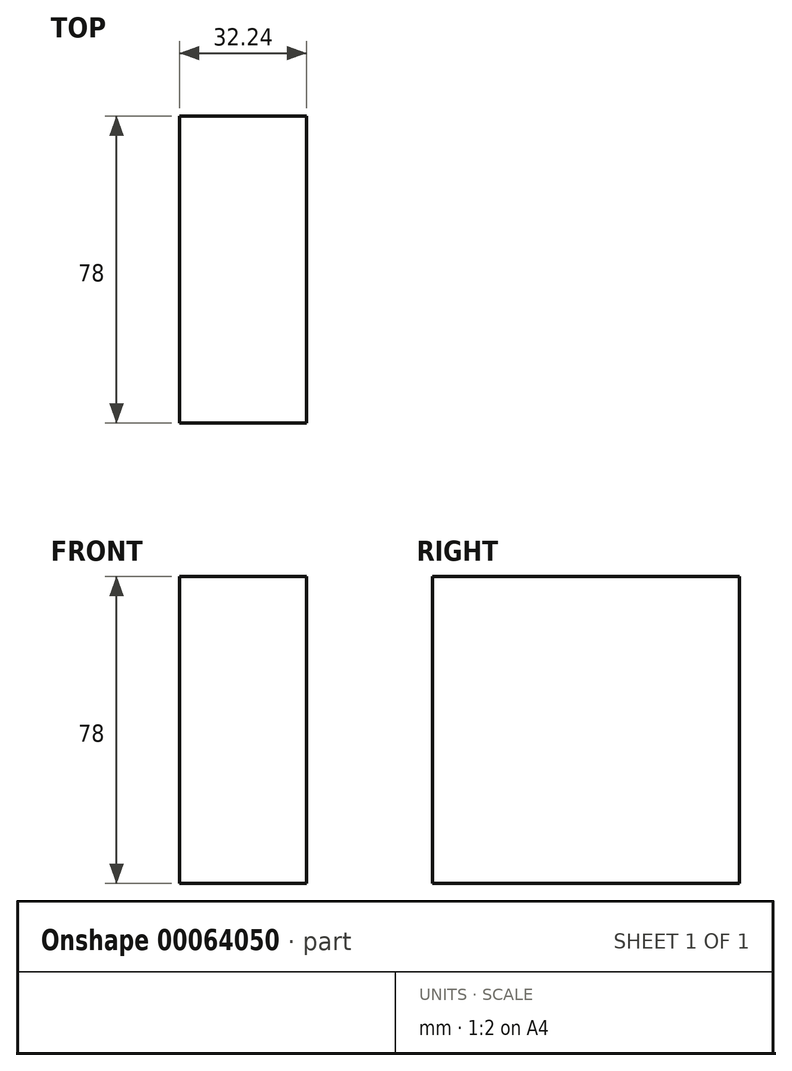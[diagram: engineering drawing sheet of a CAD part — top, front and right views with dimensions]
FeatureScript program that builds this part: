
annotation { "Feature Type Name" : "Feature", "Feature Type Description" : "" }
export const myFeature = defineFeature(function(context is Context, id is Id, definition is map)
    precondition{}
    {
        {
            var Q0;
            Q0=qCreatedBy(makeId("Right.planeOp"),FACE);
            var sketch = newSketch(context, id + "F0", { "sketchPlane" : qUnion([Q0])});
            skLineSegment(sketch, "E0.rect.bottom", {"start": v(39, 39) * mm, "end": v(-39, 39) * mm});
            skLineSegment(sketch, "E0.rect.top", {"start": v(39, -39) * mm, "end": v(-39, -39) * mm});
            skLineSegment(sketch, "E0.rect.left", {"start": v(39, 39) * mm, "end": v(39, -39) * mm});
            skLineSegment(sketch, "E0.rect.right", {"start": v(-39, 39) * mm, "end": v(-39, -39) * mm});
            skPoint(sketch, "E0.rect.middle", {"position": v(0, 0) * mm});
            skSolve(sketch);
        }
        {
            var Q0;
            Q0 = qSketchRegion(id + "F0", true);
            extrude(context, id + "F1", {"entities" : qUnion([Q0]), "endBound" : BoundingType.SYMMETRIC, "depth" : 32.25 * mm});
        }
    });
